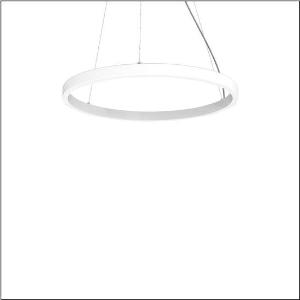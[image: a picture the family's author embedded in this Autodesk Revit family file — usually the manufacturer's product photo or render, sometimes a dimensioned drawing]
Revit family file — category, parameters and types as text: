
# Revit family: silica_r__21_ring-o_5pjbo3d3004a_bcd7
name_source: partatom
category: Lighting Fixtures
units: mm (PartAtom-declared; Revit-internal decimal feet)

## family parameters
Cut with Voids When Loaded = No
Host = Face
Light Source = No
Part Type = Normal
Room Calculation Point = No
Round Connector Dimension = Use Diameter
Shared = No

## types (1)
- Silica® 21 Ring-O (1 x LED, 7210 lm, 105 W, 4000K)
    Apparent Load = 105 VA
    CIE Flux Codes = 2 16 49 50 100
    Color Rendering = 80
    Color Temperature = 4000K
    Default Elevation = 1800 mm
    Description = Silica® 21 Ring-O, suspended luminaire, of PMMA, frosted, light emission: outer ring side luminous distribution, primary light characteristic: symmetric, installation type: suspended mounting, LED, rated luminous flux: 7.210lm, luminous efficacy: 69lm/W, light colour: 840, colour temperature: 4000K, with terminal, 5-pole, mains connection: 230V, AC/DC, 0/50..60Hz, rated input power: 105W, housing, of extruded aluminium section, traffic white (RAL 9016), diameter: 1.100mm, ceiling canopy, traffic white (RAL 9016), protection rating (lamp compartment): IP40, insulation class (complete): insulation class I (protective earthing), certification: CE, impact resistance: IK02, permissible operating ambient temperature: 0..+35°C, packaging unit: 1 piece
    Height = 48 mm  [stored 0.15748 ft]
    Lamp = 1 x LED
    Lamp Light Flux = 7210 lm
    Lamp Power = 105 W
    Lamp count = 1
    Length = 1100 mm
    Luminous efficacy = 69 lm/W
    Manufacturer = Siteco
    ModVariant = No
    Model = 5PJBO3D3004A
    Mounting Place = Ceiling
    Mounting Type = Pendant
    Number of Poles = 1
    OnlyDefault = Yes
    Power Factor = 1
    Product Name = Silica® 21 Ring-O
    Product group = suspended luminaire
    ProductGroupID = 904
    Protection Class = Protection class I
    Protection Degree = Degree of protection
    RLX_Detail_Level = 1
    RLX_Emergency_Light_Flux = 0 lm
    RLX_Emergency_Type = 0
    RLX_Emergency_Type_DB = No
    RlxData = <blob elided: 13513 chars, md5=443f95a9>
    Socket = socket
    Standby Power = 0 W
    System Light Flux = 7210 lm
    System Power = 105 W
    Type Comments = Product without accessories
    Type Image = l_1258387.jpg
    URL = http://relux.com
    VarID = ---
    Voltage = 0 V
    Weight = 0.00 kg
    Width = 0 mm  [stored 0 ft]

note: [stored X ft] marks values corroborated as IEEE doubles in the binary element streams (Revit-internal decimal feet)

## geometry (parser evidence)
native form markers: Sweep x10
no freeform markers — native parametric forms only
